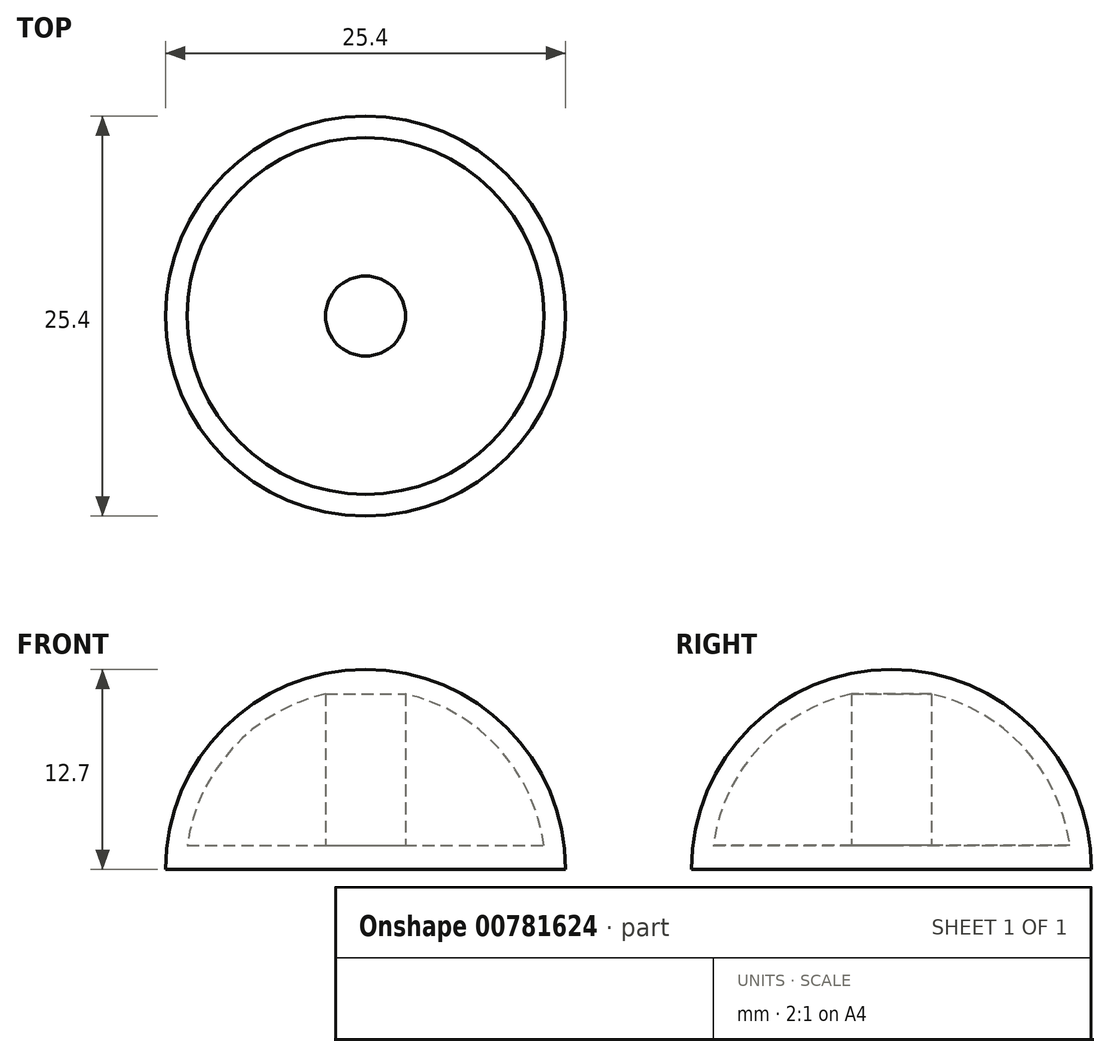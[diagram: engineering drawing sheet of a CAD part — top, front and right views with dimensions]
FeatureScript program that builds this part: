
annotation { "Feature Type Name" : "Feature", "Feature Type Description" : "" }
export const myFeature = defineFeature(function(context is Context, id is Id, definition is map)
    precondition{}
    {
        {
            var Q0;
            Q0=qCreatedBy(makeId("Top.planeOp"),FACE);
            var sketch = newSketch(context, id + "F0", { "sketchPlane" : qUnion([Q0])});
            skCircle(sketch, "E0", {"center": v(0, 0) * mm, "radius": 12.7 * mm});
            skLineSegment(sketch, "E1", {"start": v(0, 12.7) * mm, "end": v(0, -12.7) * mm});
            skSolve(sketch);
        }
        {
            var Q0;
            {var subQ0=sQuery(id+"F0.wireOp",EDGE,"E1");Q0=makeQuery(id+"F0.imprint","IMPRINT",FACE,{"disambiguationData":[TD([[makeQuery(id+"F0.imprint","IMPRINT",EDGE,{"derivedFrom":subQ0}),1.0]])]});}
            var Q1;
            Q1=sQuery(id+"F0.wireOp",EDGE,"E1");
            revolve(context, id + "F1", {"surfaceOperationType" : NewSurfaceOperationType.NEW, "entities" : qUnion([Q0]), "axis" : qUnion([Q1]), "revolveType" : RevolveType.ONE_DIRECTION, "angle" : 180 * degree});
        }
        {
            var Q0;
            Q0=makeQuery(id+"F1.opRevolve","CAP_FACE",FACE,{"disambiguationData":[OSD([sQuery(id+"F0.wireOp",EDGE,"E0"),sQuery(id+"F0.wireOp",EDGE,"E1")])],"isStart":true});
            var sketch = newSketch(context, id + "F2", { "sketchPlane" : qUnion([Q0])});
            skCircle(sketch, "E2", {"center": v(0, 0) * mm, "radius": 11.43 * mm});
            skLineSegment(sketch, "E3", {"start": v(0, 11.43) * mm, "end": v(0, -11.43) * mm});
            skSolve(sketch);
        }
        {
            var Q0;
            {var subQ0=sQuery(id+"F2.wireOp",EDGE,"E3");Q0=makeQuery(id+"F2.imprint","IMPRINT",FACE,{"disambiguationData":[TD([[makeQuery(id+"F2.imprint","IMPRINT",EDGE,{"derivedFrom":subQ0}),1.0]])]});}
            var Q1;
            Q1=sQuery(id+"F2.wireOp",EDGE,"E3");
            revolve(context, id + "F3", {"operationType" : NewBodyOperationType.REMOVE, "surfaceOperationType" : NewSurfaceOperationType.NEW, "entities" : qUnion([Q0]), "axis" : qUnion([Q1]), "revolveType" : RevolveType.FULL, "oppositeDirection" : true});
        }
        {
            var Q0;
            Q0=makeQuery(id+"F1.opRevolve","CAP_FACE",FACE,{"disambiguationData":[OSD([sQuery(id+"F0.wireOp",EDGE,"E0"),sQuery(id+"F0.wireOp",EDGE,"E1")])],"isStart":true});
            var sketch = newSketch(context, id + "F4", { "sketchPlane" : qUnion([Q0])});
            skCircle(sketch, "E4", {"center": v(0, 0) * mm, "radius": 2.54 * mm});
            skSolve(sketch);
        }
        {
            var Q0;
            Q0=makeQuery(id+"F4.imprint","IMPRINT",FACE,{"disambiguationData":[TD([[makeQuery(id+"F4.imprint","IMPRINT",EDGE,{"derivedFrom":sQuery(id+"F4.wireOp",EDGE,"E4")}),1.0]])]});
            extrude(context, id + "F5", {"entities" : qUnion([Q0]), "operationType" : NewBodyOperationType.ADD, "endBound" : BoundingType.UP_TO_NEXT, "oppositeDirection" : true, "depth" : 25.4 * mm, "offsetDistance" : 25.4 * mm});
        }
        {
            var Q0;
            Q0=makeQuery(id+"F5.opExtrude","CAP_FACE",FACE,{"disambiguationData":[OSD([sQuery(id+"F4.wireOp",EDGE,"E4")])],"isStart":true});
            var sketch = newSketch(context, id + "F6", { "sketchPlane" : qUnion([Q0])});
            skCircle(sketch, "E5", {"center": v(0, 0) * mm, "radius": 11.43 * mm});
            skSolve(sketch);
        }
        {
            var Q0;
            Q0=makeQuery(id+"F6.imprint","IMPRINT",FACE,{"disambiguationData":[TD([[makeQuery(id+"F6.imprint","IMPRINT",EDGE,{"derivedFrom":sQuery(id+"F6.wireOp",EDGE,"E5")}),1.0]])]});
            extrude(context, id + "F7", {"entities" : qUnion([Q0]), "operationType" : NewBodyOperationType.ADD, "oppositeDirection" : true, "depth" : 1.52 * mm, "offsetDistance" : 25.4 * mm});
        }
    });
